# Revit family: Window_M600-Awining-Crank_Quaker
name_source: partatom
category: Windows
units: mm (PartAtom-declared; Revit-internal decimal feet)

## family parameters
Always vertical = No
Classification Number = 23.30.20.00
Cut with Voids When Loaded = No
Host = Wall
Room Calculation Point = No
Shared = No

## types (2) — shared parameters
Analytic Construction = <None>
Default Sill Height = 12 "
Frame Material = Powder Coat - Quaker - White
Glass Material = Glass - Quaker - Insulated
Height = 36 "
Installation-Fabrication = https://www.quakercommercialwindows.com
Keynote = 08 51 13
Manufacturer = Quaker Windows & Doors
Model = M600 Awning Crank Bar
Rough Height = 36 "
Rough Width = 24 "
URL = https://www.quakercommercialwindows.com
Wall Closure = By host
Width = 24 "
to backside of fin = 1.312 "
zero-valued in all types: Cost

## per-type parameters (varying)
| type | Bevel Exterior | Description | Squared Off Exterior |
| 24" x 36", Bevel Exterior | Yes | Awning Window, Single, Bevel Exterior | No |
| 24" x 36", Squared Off Exterior | No | Awning Window, Single, Squared Off Exterior | Yes |

## geometry (parser evidence)
native form markers: Sweep x7
no freeform markers — native parametric forms only
